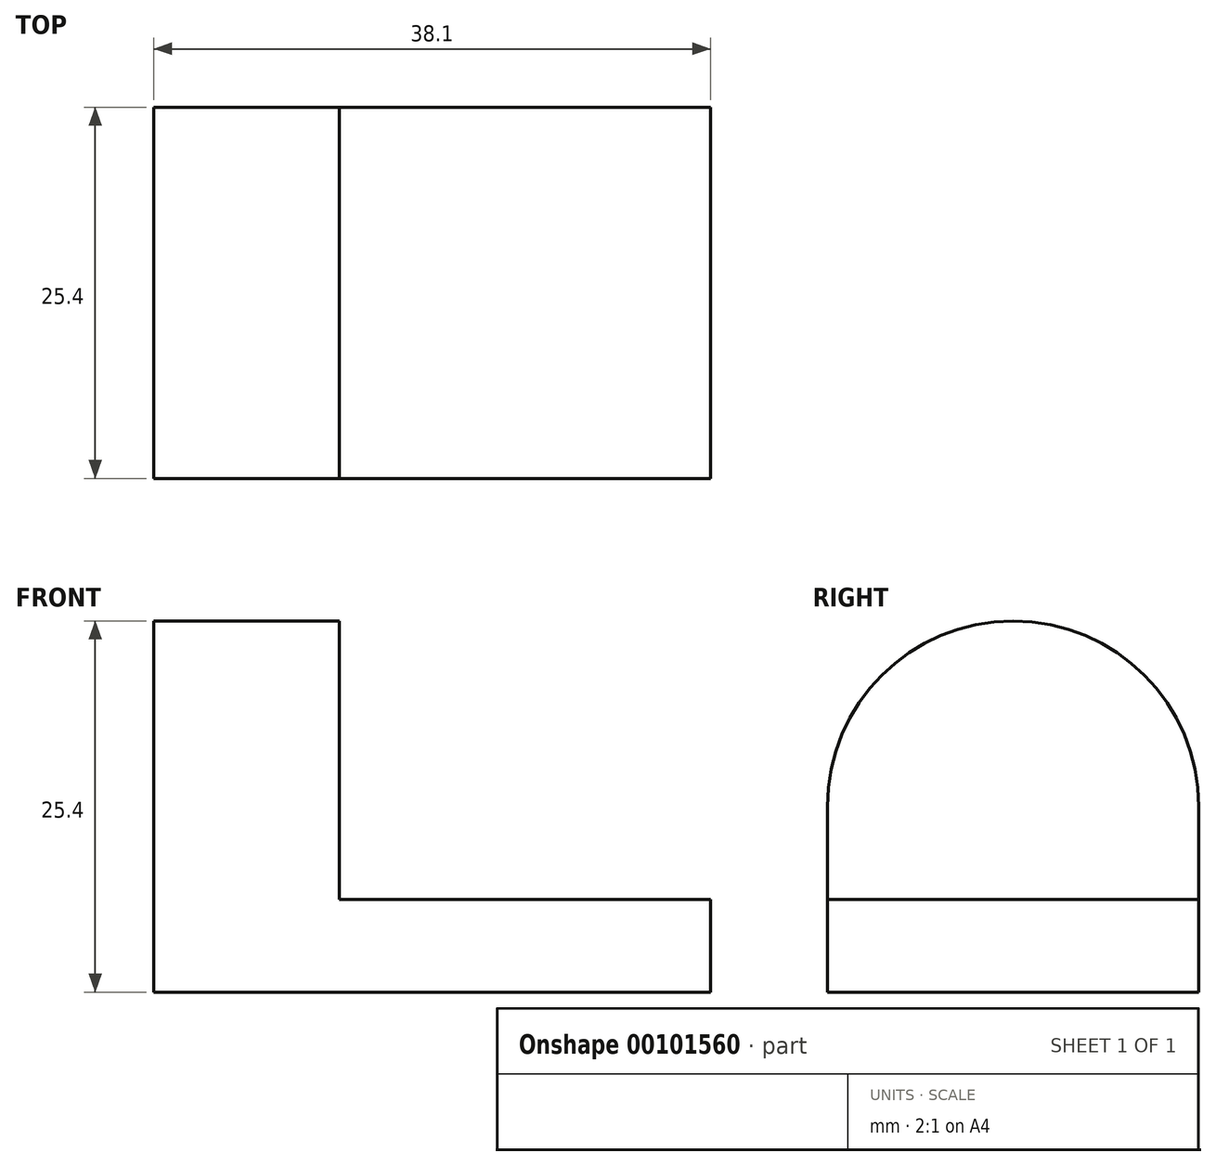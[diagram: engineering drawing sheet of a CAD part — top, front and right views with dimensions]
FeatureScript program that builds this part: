
annotation { "Feature Type Name" : "Feature", "Feature Type Description" : "" }
export const myFeature = defineFeature(function(context is Context, id is Id, definition is map)
    precondition{}
    {
        {
            var Q0;
            Q0=qCreatedBy(makeId("Right.planeOp"),FACE);
            var sketch = newSketch(context, id + "F0", { "sketchPlane" : qUnion([Q0])});
            skLineSegment(sketch, "E0", {"start": v(0, 0) * mm, "end": v(0, 12.7) * mm});
            skLineSegment(sketch, "E1", {"start": v(0, 0) * mm, "end": v(25.4, 0) * mm});
            skLineSegment(sketch, "E2", {"start": v(25.4, 0) * mm, "end": v(25.4, 12.7) * mm});
            skArc(sketch, "E3", {"start": v(25.4, 12.7) * mm, "mid": v(12.7, 25.4) * mm, "end": v(0, 12.7) * mm});
            skSolve(sketch);
        }
        {
            var Q0;
            Q0=makeQuery(id+"F0.imprint","IMPRINT",FACE,{"disambiguationData":[TD([[makeQuery(id+"F0.imprint","IMPRINT",EDGE,{"derivedFrom":sQuery(id+"F0.wireOp",EDGE,"E0")}),-1.0]])]});
            extrude(context, id + "F1", {"entities" : qUnion([Q0]), "depth" : 12.7 * mm});
        }
        {
            var Q0;
            Q0=qCreatedBy(makeId("Front.planeOp"),FACE);
            var sketch = newSketch(context, id + "F2", { "sketchPlane" : qUnion([Q0])});
            skLineSegment(sketch, "E4.bottom", {"start": v(0, 0) * mm, "end": v(38.1, 0) * mm});
            skLineSegment(sketch, "E4.top", {"start": v(0, 6.35) * mm, "end": v(38.1, 6.35) * mm});
            skLineSegment(sketch, "E4.left", {"start": v(0, 0) * mm, "end": v(0, 6.35) * mm});
            skLineSegment(sketch, "E4.right", {"start": v(38.1, 0) * mm, "end": v(38.1, 6.35) * mm});
            skSolve(sketch);
        }
        {
            var Q0;
            Q0 = qSketchRegion(id + "F2", true);
            extrude(context, id + "F3", {"entities" : qUnion([Q0]), "operationType" : NewBodyOperationType.ADD, "oppositeDirection" : true, "depth" : 25.4 * mm});
        }
    });
